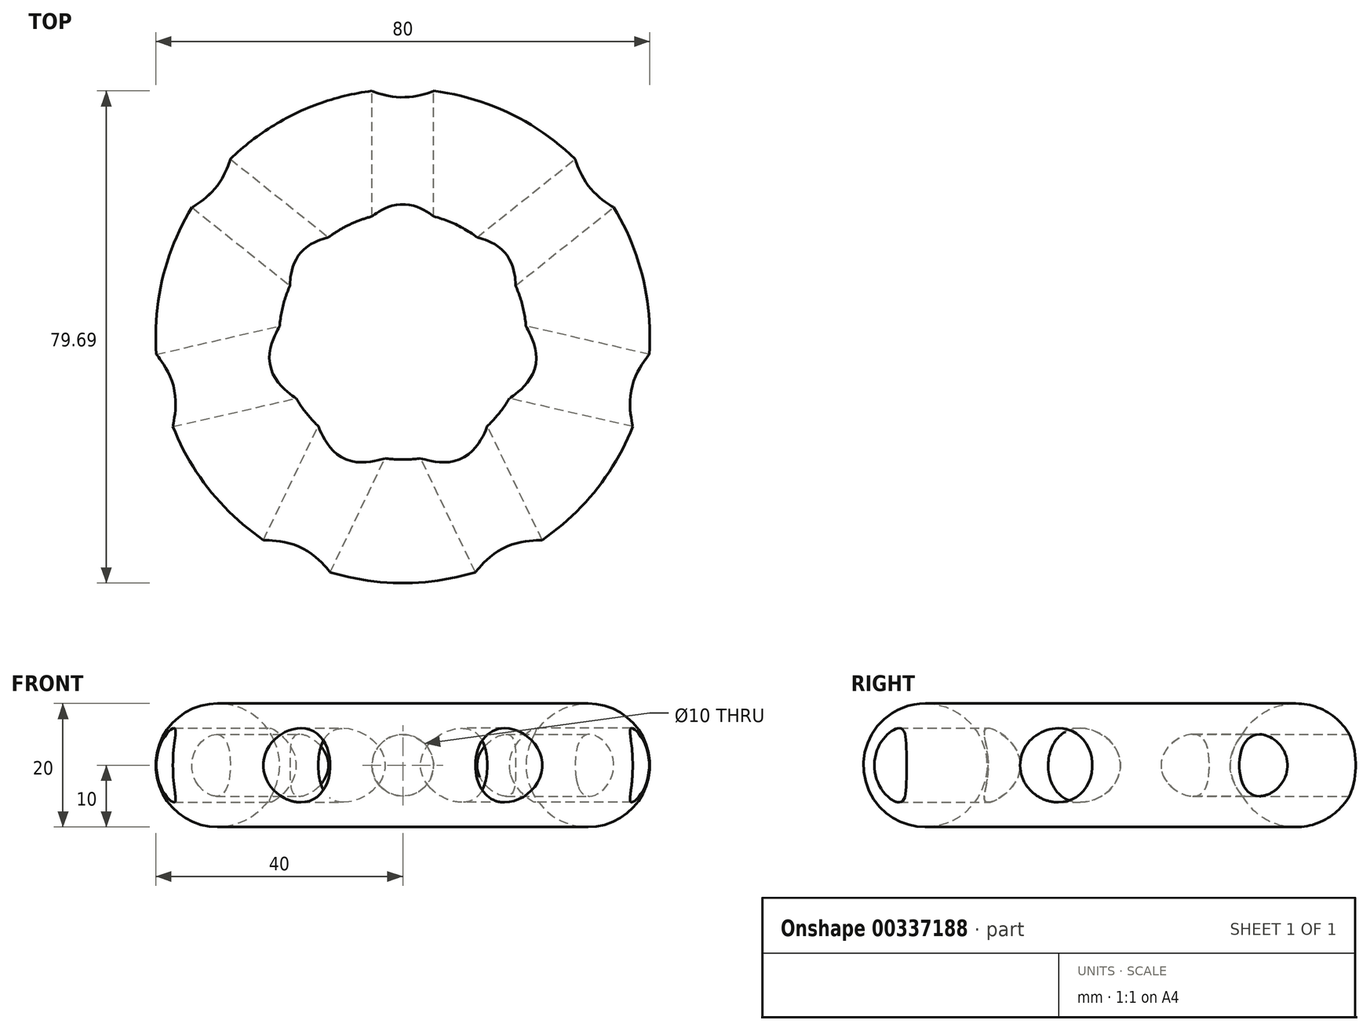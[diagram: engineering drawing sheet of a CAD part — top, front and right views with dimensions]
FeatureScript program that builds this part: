
annotation { "Feature Type Name" : "Feature", "Feature Type Description" : "" }
export const myFeature = defineFeature(function(context is Context, id is Id, definition is map)
    precondition{}
    {
        {
            var Q0;
            Q0=qCreatedBy(makeId("Front.planeOp"),FACE);
            var sketch = newSketch(context, id + "F0", { "sketchPlane" : qUnion([Q0])});
            skCircle(sketch, "E0", {"center": v(-30, 0) * mm, "radius": 10 * mm});
            skLineSegment(sketch, "E1", {"start": v(0, 0) * mm, "end": v(0, 40) * mm});
            skLineSegment(sketch, "E2", {"start": v(0, 0) * mm, "end": v(0, -40) * mm});
            skSolve(sketch);
        }
        {
            var Q0;
            Q0=makeQuery(id+"F0.imprint","IMPRINT",FACE,{"disambiguationData":[TD([[makeQuery(id+"F0.imprint","IMPRINT",EDGE,{"derivedFrom":sQuery(id+"F0.wireOp",EDGE,"E0")}),1.0]])]});
            var Q1;
            Q1=sQuery(id+"F0.wireOp",EDGE,"E1");
            revolve(context, id + "F1", {"entities" : qUnion([Q0]), "axis" : qUnion([Q1]), "revolveType" : RevolveType.FULL});
        }
        {
            var Q0;
            Q0=qCreatedBy(makeId("Top.planeOp"),FACE);
            var sketch = newSketch(context, id + "F2", { "sketchPlane" : qUnion([Q0])});
            skCircle(sketch, "E3", {"center": v(0, 0) * mm, "radius": 40 * mm});
            skLineSegment(sketch, "E4", {"start": v(0, 40) * mm, "end": v(0, 0) * mm});
            skLineSegment(sketch, "E5.1.0", {"start": v(-31.27, 24.94) * mm, "end": v(0, 0) * mm});
            skLineSegment(sketch, "E5.2.0", {"start": v(-39, -8.9) * mm, "end": v(0, 0) * mm});
            skLineSegment(sketch, "E6.1.3.0", {"start": v(-17.36, -36.04) * mm, "end": v(0, 0) * mm});
            skLineSegment(sketch, "E6.1.4.0", {"start": v(17.36, -36.04) * mm, "end": v(0, 0) * mm});
            skLineSegment(sketch, "E6.1.5.0", {"start": v(39, -8.9) * mm, "end": v(0, 0) * mm});
            skLineSegment(sketch, "E6.1.6.0", {"start": v(31.27, 24.94) * mm, "end": v(0, 0) * mm});
            skLineSegment(sketch, "E7.bottom", {"start": v(0, 40) * mm, "end": v(-5, 40) * mm});
            skLineSegment(sketch, "E7.top", {"start": v(0, 15) * mm, "end": v(-5, 15) * mm});
            skLineSegment(sketch, "E7.left", {"start": v(0, 40) * mm, "end": v(0, 15) * mm});
            skLineSegment(sketch, "E7.right", {"start": v(-5, 40) * mm, "end": v(-5, 15) * mm});
            skLineSegment(sketch, "E8.bottom", {"start": v(0, 40) * mm, "end": v(6, 40) * mm});
            skLineSegment(sketch, "E8.top", {"start": v(0, 15) * mm, "end": v(6, 15) * mm});
            skLineSegment(sketch, "E8.right", {"start": v(6, 40) * mm, "end": v(6, 15) * mm});
            skLineSegment(sketch, "E9.1.0", {"start": v(-27.53, 29.63) * mm, "end": v(-7.99, 14.04) * mm});
            skLineSegment(sketch, "E9.2.0", {"start": v(-40.33, -3.05) * mm, "end": v(-15.96, 2.51) * mm});
            skLineSegment(sketch, "E10.2.3.0", {"start": v(-22.76, -33.44) * mm, "end": v(-11.91, -10.91) * mm});
            skLineSegment(sketch, "E10.2.4.0", {"start": v(11.95, -38.64) * mm, "end": v(1.1, -16.12) * mm});
            skLineSegment(sketch, "E10.2.5.0", {"start": v(37.66, -14.75) * mm, "end": v(13.29, -9.19) * mm});
            skLineSegment(sketch, "E10.2.6.0", {"start": v(35.01, 20.25) * mm, "end": v(15.47, 4.66) * mm});
            skLineSegment(sketch, "E11", {"start": v(-27.53, 29.63) * mm, "end": v(-31.27, 24.94) * mm});
            skLineSegment(sketch, "E12", {"start": v(-7.99, 14.04) * mm, "end": v(-11.73, 9.35) * mm});
            skLineSegment(sketch, "E13", {"start": v(-15.96, 2.51) * mm, "end": v(-14.62, -3.34) * mm});
            skLineSegment(sketch, "E14", {"start": v(-11.91, -10.91) * mm, "end": v(-6.5, -13.51) * mm});
            skLineSegment(sketch, "E15", {"start": v(1.1, -16.12) * mm, "end": v(6.5, -13.51) * mm});
            skLineSegment(sketch, "E16", {"start": v(13.29, -9.19) * mm, "end": v(14.62, -3.34) * mm});
            skLineSegment(sketch, "E17", {"start": v(15.47, 4.66) * mm, "end": v(11.73, 9.35) * mm});
            skLineSegment(sketch, "E18", {"start": v(37.66, -14.75) * mm, "end": v(39, -8.9) * mm});
            skLineSegment(sketch, "E19", {"start": v(35.01, 20.25) * mm, "end": v(31.27, 24.94) * mm});
            skLineSegment(sketch, "E20", {"start": v(-39, -8.9) * mm, "end": v(-40.33, -3.05) * mm});
            skLineSegment(sketch, "E21", {"start": v(-17.36, -36.04) * mm, "end": v(-22.76, -33.44) * mm});
            skLineSegment(sketch, "E22", {"start": v(-31.27, 24.94) * mm, "end": v(-34.4, 21.03) * mm});
            skLineSegment(sketch, "E23", {"start": v(-34.4, 21.03) * mm, "end": v(-14.84, 5.44) * mm});
            skLineSegment(sketch, "E24", {"start": v(-14.84, 5.44) * mm, "end": v(-11.73, 9.35) * mm});
            skLineSegment(sketch, "E25", {"start": v(31.27, 24.94) * mm, "end": v(28.16, 28.85) * mm});
            skLineSegment(sketch, "E26", {"start": v(28.16, 28.85) * mm, "end": v(8.61, 13.26) * mm});
            skLineSegment(sketch, "E27", {"start": v(8.61, 13.26) * mm, "end": v(11.73, 9.35) * mm});
            skSolve(sketch);
        }
        {
            var Q0;
            {var subQ3=sQuery(id+"F2.wireOp",EDGE,"E27");Q0=makeQuery(id+"F2.imprint","IMPRINT",FACE,{"disambiguationData":[TD([[makeQuery(id+"F2.imprint","IMPRINT",EDGE,{"derivedFrom":subQ3}),1.0]])]});}
            var Q1;
            Q1=sQuery(id+"F2.wireOp",EDGE,"E6.1.6.0");
            revolve(context, id + "F3", {"operationType" : NewBodyOperationType.REMOVE, "entities" : qUnion([Q0]), "axis" : qUnion([Q1]), "revolveType" : RevolveType.FULL});
        }
        {
            var Q0;
            {var subQ4=sQuery(id+"F2.wireOp",EDGE,"E7.top");Q0=makeQuery(id+"F2.imprint","IMPRINT",FACE,{"disambiguationData":[TD([[makeQuery(id+"F2.imprint","IMPRINT",EDGE,{"derivedFrom":subQ4}),-1.0]])]});}
            var Q1;
            Q1=sQuery(id+"F2.wireOp",EDGE,"E4");
            revolve(context, id + "F4", {"operationType" : NewBodyOperationType.REMOVE, "entities" : qUnion([Q0]), "axis" : qUnion([Q1]), "revolveType" : RevolveType.FULL});
        }
        {
            var Q0;
            {var subQ3=sQuery(id+"F2.wireOp",EDGE,"E24");Q0=makeQuery(id+"F2.imprint","IMPRINT",FACE,{"disambiguationData":[TD([[makeQuery(id+"F2.imprint","IMPRINT",EDGE,{"derivedFrom":subQ3}),1.0]])]});}
            var Q1;
            Q1=sQuery(id+"F2.wireOp",EDGE,"E5.1.0");
            revolve(context, id + "F5", {"operationType" : NewBodyOperationType.REMOVE, "entities" : qUnion([Q0]), "axis" : qUnion([Q1]), "revolveType" : RevolveType.FULL, "oppositeDirection" : true});
        }
        {
            var Q0;
            {var subQ3=sQuery(id+"F2.wireOp",EDGE,"E13");Q0=makeQuery(id+"F2.imprint","IMPRINT",FACE,{"disambiguationData":[TD([[makeQuery(id+"F2.imprint","IMPRINT",EDGE,{"derivedFrom":subQ3}),-1.0]])]});}
            var Q1;
            Q1=sQuery(id+"F2.wireOp",EDGE,"E5.2.0");
            revolve(context, id + "F6", {"operationType" : NewBodyOperationType.REMOVE, "entities" : qUnion([Q0]), "axis" : qUnion([Q1]), "revolveType" : RevolveType.FULL, "oppositeDirection" : true});
        }
        {
            var Q0;
            {var subQ3=sQuery(id+"F2.wireOp",EDGE,"E14");Q0=makeQuery(id+"F2.imprint","IMPRINT",FACE,{"disambiguationData":[TD([[makeQuery(id+"F2.imprint","IMPRINT",EDGE,{"derivedFrom":subQ3}),-1.0]])]});}
            var Q1;
            Q1=sQuery(id+"F2.wireOp",EDGE,"E6.1.3.0");
            revolve(context, id + "F7", {"operationType" : NewBodyOperationType.REMOVE, "entities" : qUnion([Q0]), "axis" : qUnion([Q1]), "revolveType" : RevolveType.FULL, "oppositeDirection" : true});
        }
        {
            var Q0;
            {var subQ3=sQuery(id+"F2.wireOp",EDGE,"E15");Q0=makeQuery(id+"F2.imprint","IMPRINT",FACE,{"disambiguationData":[TD([[makeQuery(id+"F2.imprint","IMPRINT",EDGE,{"derivedFrom":subQ3}),-1.0]])]});}
            var Q1;
            Q1=sQuery(id+"F2.wireOp",EDGE,"E6.1.4.0");
            revolve(context, id + "F8", {"operationType" : NewBodyOperationType.REMOVE, "entities" : qUnion([Q0]), "axis" : qUnion([Q1]), "revolveType" : RevolveType.FULL, "oppositeDirection" : true});
        }
        {
            var Q0;
            {var subQ3=sQuery(id+"F2.wireOp",EDGE,"E16");Q0=makeQuery(id+"F2.imprint","IMPRINT",FACE,{"disambiguationData":[TD([[makeQuery(id+"F2.imprint","IMPRINT",EDGE,{"derivedFrom":subQ3}),-1.0]])]});}
            var Q1;
            Q1=sQuery(id+"F2.wireOp",EDGE,"E6.1.5.0");
            revolve(context, id + "F9", {"operationType" : NewBodyOperationType.REMOVE, "entities" : qUnion([Q0]), "axis" : qUnion([Q1]), "revolveType" : RevolveType.FULL, "oppositeDirection" : true});
        }
    });
